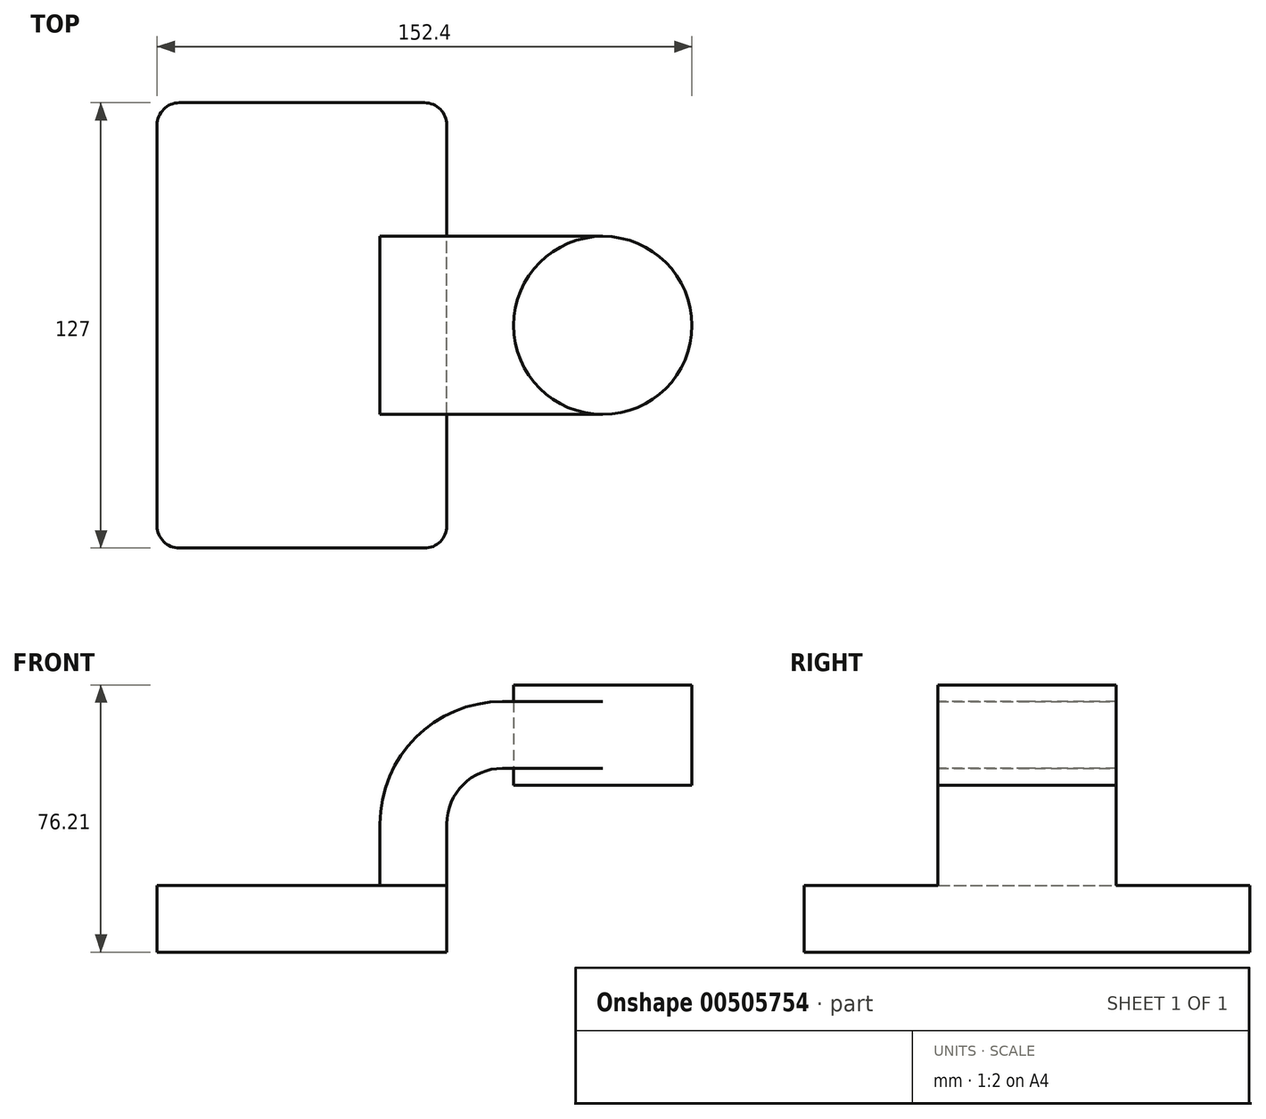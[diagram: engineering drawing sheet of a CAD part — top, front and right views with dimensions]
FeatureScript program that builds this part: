
annotation { "Feature Type Name" : "Feature", "Feature Type Description" : "" }
export const myFeature = defineFeature(function(context is Context, id is Id, definition is map)
    precondition{}
    {
        {
            var Q0;
            Q0=qCreatedBy(makeId("Front.planeOp"),FACE);
            var sketch = newSketch(context, id + "F0", { "sketchPlane" : qUnion([Q0])});
            skPoint(sketch, "E0.middle", {"position": v(0, 0) * mm});
            skLineSegment(sketch, "E1.bottom", {"start": v(111.13, 38.1) * mm, "end": v(60.32, 38.1) * mm});
            skLineSegment(sketch, "E1.top", {"start": v(111.13, 66.67) * mm, "end": v(60.32, 66.67) * mm});
            skLineSegment(sketch, "E1.left", {"start": v(111.12, 38.1) * mm, "end": v(111.12, 66.68) * mm});
            skLineSegment(sketch, "E1.right", {"start": v(60.32, 38.1) * mm, "end": v(60.32, 66.68) * mm});
            skPoint(sketch, "E1.middle", {"position": v(85.72, 52.39) * mm});
            skLineSegment(sketch, "E2.bottom", {"start": v(41.28, -9.52) * mm, "end": v(-41.28, -9.52) * mm});
            skLineSegment(sketch, "E2.top", {"start": v(41.28, 9.53) * mm, "end": v(-41.28, 9.53) * mm});
            skLineSegment(sketch, "E2.left", {"start": v(41.28, -9.52) * mm, "end": v(41.28, 9.53) * mm});
            skLineSegment(sketch, "E2.right", {"start": v(-41.28, -9.52) * mm, "end": v(-41.28, 9.53) * mm});
            skLineSegment(sketch, "E3", {"start": v(41.27, 9.53) * mm, "end": v(41.27, 27) * mm});
            skArc(sketch, "E4", {"start": v(41.27, 27) * mm, "mid": v(45.92, 38.23) * mm, "end": v(57.15, 42.88) * mm});
            skLineSegment(sketch, "E5", {"start": v(57.15, 42.88) * mm, "end": v(85.72, 42.88) * mm});
            skLineSegment(sketch, "E6.0", {"start": v(57.15, 61.93) * mm, "end": v(85.72, 61.93) * mm});
            skArc(sketch, "E6.1", {"start": v(22.22, 27) * mm, "mid": v(32.45, 51.7) * mm, "end": v(57.15, 61.93) * mm});
            skLineSegment(sketch, "E6.2", {"start": v(22.22, 9.53) * mm, "end": v(22.22, 27) * mm});
            skLineSegment(sketch, "E7", {"start": v(85.72, 38.1) * mm, "end": v(85.72, 66.67) * mm});
            skFitSpline(sketch, "E8", {"points": [v(-41.28, 9.53) * mm, v(60.32, 66.68) * mm], "startDerivative": vector(40.26, 92.26) * mm, "endDerivative": vector(194.85, -5.22) * mm});
            skSolve(sketch);
        }
        {
            var Q0;
            Q0=makeQuery(id+"F0.imprint","IMPRINT",FACE,{"disambiguationData":[TD([[makeQuery(id+"F0.imprint","IMPRINT",EDGE,{"derivedFrom":sQuery(id+"F0.wireOp",EDGE,"E2.bottom")}),-1.0]])]});
            extrude(context, id + "F1", {"entities" : qUnion([Q0]), "endBound" : BoundingType.SYMMETRIC, "depth" : 127 * mm});
        }
        {
            var Q0;
            {var subQ0=sQuery(id+"F0.wireOp",EDGE,"E5");var subQ1=sQuery(id+"F0.wireOp",EDGE,"E1.right");var subQ2=makeQuery(id+"F0.imprint","INTERSECT",VERTEX,{"derivedFrom":[subQ1,subQ0]});Q0=makeQuery(id+"F0.imprint","IMPRINT",FACE,{"disambiguationData":[TD([[makeQuery(id+"F0.imprint","IMPRINT",EDGE,{"disambiguationData":[TD([[subQ2,-1.0]])],"derivedFrom":subQ1}),-1.0]])]});}
            var Q1;
            {var subQ0=sQuery(id+"F0.wireOp",EDGE,"E3");Q1=makeQuery(id+"F0.imprint","IMPRINT",FACE,{"disambiguationData":[TD([[makeQuery(id+"F0.imprint","IMPRINT",EDGE,{"derivedFrom":subQ0}),1.0]])]});}
            extrude(context, id + "F2", {"entities" : qUnion([Q0, Q1]), "operationType" : NewBodyOperationType.ADD, "endBound" : BoundingType.SYMMETRIC, "depth" : 50.8 * mm});
        }
        {
            var Q0;
            {var subQ0=sQuery(id+"F0.wireOp",EDGE,"E6.1");Q0=makeQuery(id+"F0.imprint","IMPRINT",FACE,{"disambiguationData":[TD([[makeQuery(id+"F0.imprint","IMPRINT",EDGE,{"derivedFrom":subQ0}),1.0]])]});}
            extrude(context, id + "F3", {"entities" : qUnion([Q0]), "operationType" : NewBodyOperationType.ADD, "endBound" : BoundingType.SYMMETRIC, "depth" : 15.88 * mm});
        }
        {
            var Q0;
            {var subQ4=sQuery(id+"F0.wireOp",EDGE,"E1.left");Q0=makeQuery(id+"F0.imprint","IMPRINT",FACE,{"disambiguationData":[TD([[makeQuery(id+"F0.imprint","IMPRINT",EDGE,{"derivedFrom":subQ4}),1.0]])]});}
            var Q1;
            Q1=sQuery(id+"F0.wireOp",EDGE,"E7");
            revolve(context, id + "F4", {"operationType" : NewBodyOperationType.ADD, "entities" : qUnion([Q0]), "axis" : qUnion([Q1]), "revolveType" : RevolveType.FULL});
        }
        {
            var Q0;
            {var subQ4=sQuery(id+"F0.wireOp",EDGE,"E1.left");Q0=makeQuery(id+"F0.imprint","IMPRINT",FACE,{"disambiguationData":[TD([[makeQuery(id+"F0.imprint","IMPRINT",EDGE,{"derivedFrom":subQ4}),1.0]])]});}
            var Q1;
            Q1=sQuery(id+"F0.wireOp",EDGE,"E7");
            revolve(context, id + "F5", {"operationType" : NewBodyOperationType.ADD, "entities" : qUnion([Q0]), "axis" : qUnion([Q1]), "revolveType" : RevolveType.FULL});
        }
        {
            var Q0;
            {var subQ4=sQuery(id+"F0.wireOp",EDGE,"E1.left");Q0=makeQuery(id+"F0.imprint","IMPRINT",FACE,{"disambiguationData":[TD([[makeQuery(id+"F0.imprint","IMPRINT",EDGE,{"derivedFrom":subQ4}),1.0]])]});}
            var Q1;
            Q1=sQuery(id+"F0.wireOp",EDGE,"E7");
            revolve(context, id + "F6", {"entities" : qUnion([Q0]), "axis" : qUnion([Q1]), "revolveType" : RevolveType.FULL});
        }
        {
            var Q0;
            Q0=makeQuery(id+"F1.opExtrude","CAP_EDGE",EDGE,{"disambiguationData":[OSD([sQuery(id+"F0.wireOp",EDGE,"E2.left")])],"isStart":false});
            var Q1;
            Q1=makeQuery(id+"F1.opExtrude","CAP_EDGE",EDGE,{"disambiguationData":[OSD([sQuery(id+"F0.wireOp",EDGE,"E2.right")])],"isStart":false});
            var Q2;
            Q2=makeQuery(id+"F1.opExtrude","CAP_EDGE",EDGE,{"disambiguationData":[OSD([sQuery(id+"F0.wireOp",EDGE,"E2.left")])],"isStart":true});
            var Q3;
            Q3=makeQuery(id+"F1.opExtrude","CAP_EDGE",EDGE,{"disambiguationData":[OSD([sQuery(id+"F0.wireOp",EDGE,"E2.right")])],"isStart":true});
            fillet(context, id + "F7", {"entities" : qUnion([Q0, Q1, Q2, Q3]), "radius" : 6.35 * mm, "tangentPropagation" : true, "allowEdgeOverflow" : false});
        }
    });
